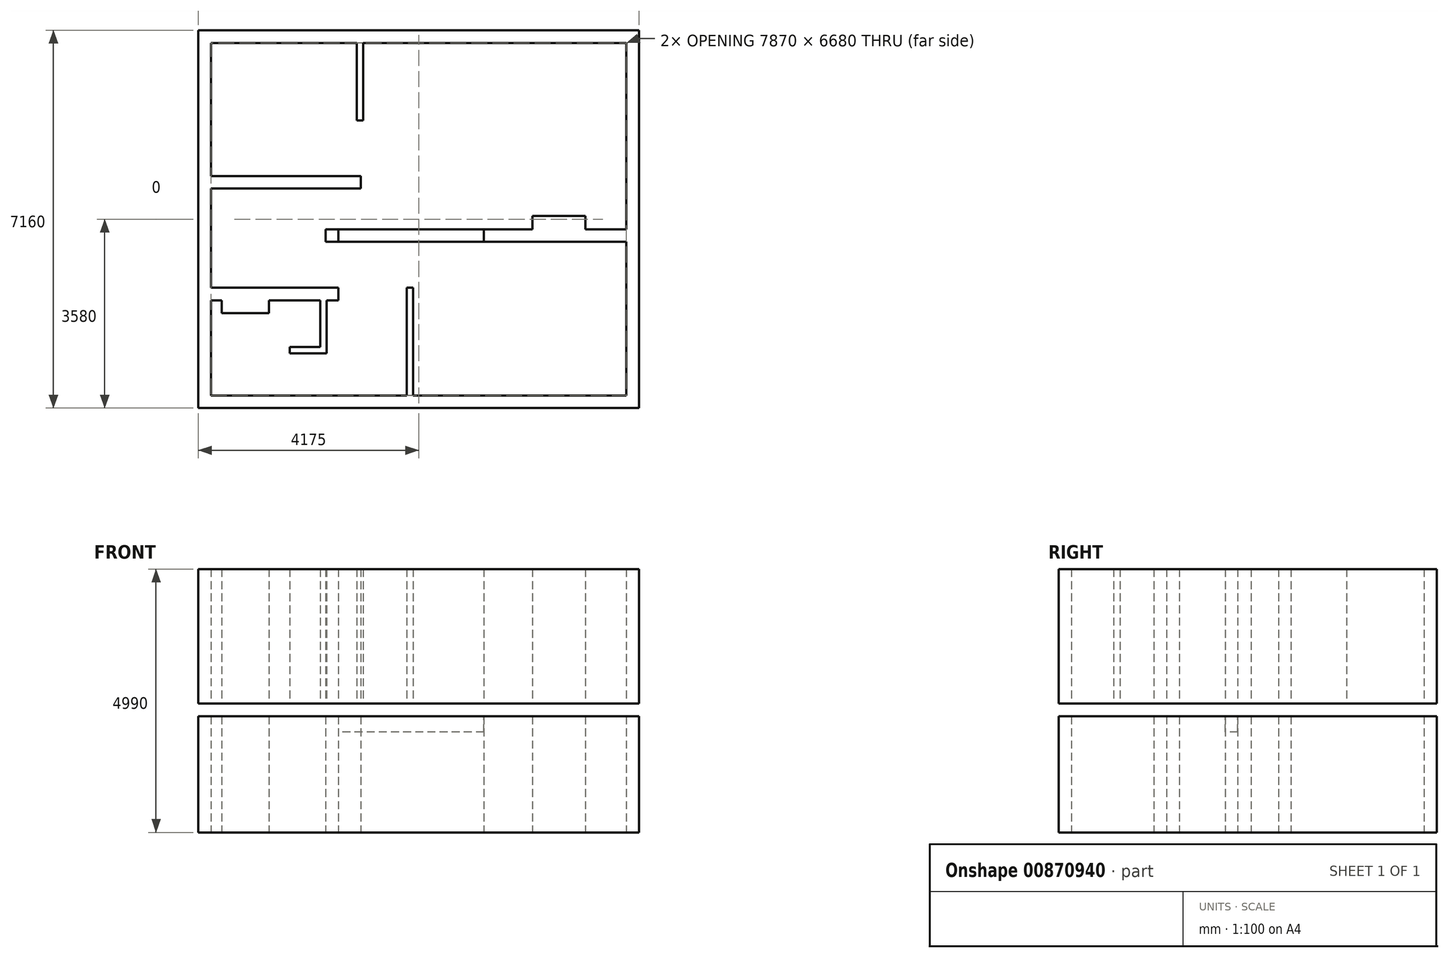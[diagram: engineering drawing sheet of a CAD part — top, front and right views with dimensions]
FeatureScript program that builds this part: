
annotation { "Feature Type Name" : "Feature", "Feature Type Description" : "" }
export const myFeature = defineFeature(function(context is Context, id is Id, definition is map)
    precondition{}
    {
        {
            var Q0;
            Q0=qCreatedBy(makeId("Top.planeOp"),FACE);
            var sketch = newSketch(context, id + "F0", { "sketchPlane" : qUnion([Q0])});
            skLineSegment(sketch, "E0.bottom", {"start": v(0, 0) * mm, "end": v(-8350, 0) * mm});
            skLineSegment(sketch, "E0.top", {"start": v(0, 7160) * mm, "end": v(-8350, 7160) * mm});
            skLineSegment(sketch, "E0.left", {"start": v(0, 0) * mm, "end": v(0, 7160) * mm});
            skLineSegment(sketch, "E0.right", {"start": v(-8350, 0) * mm, "end": v(-8350, 7160) * mm});
            skLineSegment(sketch, "E1.0", {"start": v(-240, 6920) * mm, "end": v(-8110, 6920) * mm});
            skLineSegment(sketch, "E1.1", {"start": v(-240, 240) * mm, "end": v(-240, 3150) * mm});
            skLineSegment(sketch, "E1.2", {"start": v(-240, 240) * mm, "end": v(-8110, 240) * mm});
            skLineSegment(sketch, "E1.3", {"start": v(-8110, 240) * mm, "end": v(-8110, 2040) * mm});
            skLineSegment(sketch, "E2", {"start": v(-8110, 2040) * mm, "end": v(-7910, 2040) * mm});
            skLineSegment(sketch, "E3", {"start": v(-7910, 2040) * mm, "end": v(-7910, 1800) * mm});
            skLineSegment(sketch, "E4", {"start": v(-7910, 1800) * mm, "end": v(-7010, 1800) * mm});
            skLineSegment(sketch, "E5", {"start": v(-7010, 1800) * mm, "end": v(-7010, 2040) * mm});
            skLineSegment(sketch, "E6", {"start": v(-7010, 2040) * mm, "end": v(-5700, 2040) * mm});
            skLineSegment(sketch, "E7", {"start": v(-5700, 2040) * mm, "end": v(-5700, 2280) * mm});
            skLineSegment(sketch, "E8", {"start": v(-5700, 2280) * mm, "end": v(-8110, 2280) * mm});
            skLineSegment(sketch, "E9.trimOffspring", {"start": v(-8110, 2280) * mm, "end": v(-8110, 4160) * mm});
            skLineSegment(sketch, "E10", {"start": v(-8110, 4160) * mm, "end": v(-5270, 4160) * mm});
            skLineSegment(sketch, "E11", {"start": v(-5270, 4160) * mm, "end": v(-5270, 4400) * mm});
            skLineSegment(sketch, "E12", {"start": v(-5270, 4400) * mm, "end": v(-8110, 4400) * mm});
            skLineSegment(sketch, "E13.trimOffspring", {"start": v(-8110, 4400) * mm, "end": v(-8110, 6920) * mm});
            skLineSegment(sketch, "E14", {"start": v(-240, 3150) * mm, "end": v(-2940, 3150) * mm});
            skLineSegment(sketch, "E15", {"start": v(-2940, 3150) * mm, "end": v(-2940, 3390) * mm});
            skLineSegment(sketch, "E16", {"start": v(-2940, 3390) * mm, "end": v(-2020, 3390) * mm});
            skLineSegment(sketch, "E17.trimOffspring", {"start": v(-240, 3390) * mm, "end": v(-240, 6920) * mm});
            skLineSegment(sketch, "E18", {"start": v(-2020, 3390) * mm, "end": v(-2020, 3640) * mm});
            skLineSegment(sketch, "E19", {"start": v(-2020, 3640) * mm, "end": v(-1020, 3640) * mm});
            skLineSegment(sketch, "E20", {"start": v(-1020, 3640) * mm, "end": v(-1020, 3390) * mm});
            skLineSegment(sketch, "E21.trimOffspring", {"start": v(-1020, 3390) * mm, "end": v(-240, 3390) * mm});
            skLineSegment(sketch, "E22.bottom", {"start": v(-5940, 3150) * mm, "end": v(-5700, 3150) * mm});
            skLineSegment(sketch, "E22.top", {"start": v(-5940, 3390) * mm, "end": v(-5700, 3390) * mm});
            skLineSegment(sketch, "E22.left", {"start": v(-5940, 3150) * mm, "end": v(-5940, 3390) * mm});
            skLineSegment(sketch, "E22.right", {"start": v(-5700, 3150) * mm, "end": v(-5700, 3390) * mm});
            skSolve(sketch);
        }
        {
            var Q0;
            Q0=makeQuery(id+"F0.imprint","IMPRINT",FACE,{"disambiguationData":[TD([[makeQuery(id+"F0.imprint","IMPRINT",EDGE,{"derivedFrom":sQuery(id+"F0.wireOp",EDGE,"E0.bottom")}),-1.0]])]});
            extrude(context, id + "F1", {"entities" : qUnion([Q0]), "depth" : 2200 * mm, "offsetDistance" : 25 * mm});
        }
        {
            var Q0;
            Q0=makeQuery(id+"F0.imprint","IMPRINT",FACE,{"disambiguationData":[TD([[makeQuery(id+"F0.imprint","IMPRINT",EDGE,{"derivedFrom":sQuery(id+"F0.wireOp",EDGE,"E22.bottom")}),1.0]])]});
            extrude(context, id + "F2", {"entities" : qUnion([Q0]), "depth" : 2200 * mm, "offsetDistance" : 25 * mm});
        }
        {
            var Q0;
            Q0=makeQuery(id+"F2.opExtrude","SWEPT_FACE",FACE,{"disambiguationData":[OSD([sQuery(id+"F0.wireOp",EDGE,"E22.right")])]});
            var sketch = newSketch(context, id + "F3", { "sketchPlane" : qUnion([Q0])});
            skLineSegment(sketch, "E23.0", {"start": v(3150, 2200) * mm, "end": v(3390, 2200) * mm});
            skLineSegment(sketch, "E24.0", {"start": v(3150, 2200) * mm, "end": v(3150, 0) * mm});
            skLineSegment(sketch, "E24.1", {"start": v(3390, 2200) * mm, "end": v(3390, 0) * mm});
            skLineSegment(sketch, "E25", {"start": v(3150, 1900) * mm, "end": v(3390, 1900) * mm});
            skSolve(sketch);
        }
        {
            var Q0;
            {var subQ0=sQuery(id+"F3.wireOp",EDGE,"E23.0");Q0=makeQuery(id+"F3.imprint","IMPRINT",FACE,{"disambiguationData":[TD([[makeQuery(id+"F3.imprint","IMPRINT",EDGE,{"derivedFrom":subQ0}),-1.0]])]});}
            extrude(context, id + "F4", {"entities" : qUnion([Q0]), "endBound" : BoundingType.UP_TO_NEXT, "depth" : 25 * mm, "offsetDistance" : 25 * mm});
        }
        {
            var Q0;
            Q0=makeQuery(id+"F1.opExtrude","CAP_FACE",FACE,{"disambiguationData":[OSD([sQuery(id+"F0.wireOp",EDGE,"E0.bottom"),sQuery(id+"F0.wireOp",EDGE,"E0.top"),sQuery(id+"F0.wireOp",EDGE,"E0.left"),sQuery(id+"F0.wireOp",EDGE,"E0.right"),sQuery(id+"F0.wireOp",EDGE,"E1.0"),sQuery(id+"F0.wireOp",EDGE,"E1.1"),sQuery(id+"F0.wireOp",EDGE,"E1.2"),sQuery(id+"F0.wireOp",EDGE,"E1.3"),sQuery(id+"F0.wireOp",EDGE,"E2"),sQuery(id+"F0.wireOp",EDGE,"E3"),sQuery(id+"F0.wireOp",EDGE,"E4"),sQuery(id+"F0.wireOp",EDGE,"E5"),sQuery(id+"F0.wireOp",EDGE,"E6"),sQuery(id+"F0.wireOp",EDGE,"E7"),sQuery(id+"F0.wireOp",EDGE,"E8"),sQuery(id+"F0.wireOp",EDGE,"E9.trimOffspring"),sQuery(id+"F0.wireOp",EDGE,"E10"),sQuery(id+"F0.wireOp",EDGE,"E11"),sQuery(id+"F0.wireOp",EDGE,"E12"),sQuery(id+"F0.wireOp",EDGE,"E13.trimOffspring"),sQuery(id+"F0.wireOp",EDGE,"E14"),sQuery(id+"F0.wireOp",EDGE,"E15"),sQuery(id+"F0.wireOp",EDGE,"E16"),sQuery(id+"F0.wireOp",EDGE,"E17.trimOffspring"),sQuery(id+"F0.wireOp",EDGE,"E18"),sQuery(id+"F0.wireOp",EDGE,"E19"),sQuery(id+"F0.wireOp",EDGE,"E20"),sQuery(id+"F0.wireOp",EDGE,"E21.trimOffspring")])],"isStart":false});
            cPlane(context, id + "F5", {"entities" : qUnion([Q0]), "cplaneType" : CPlaneType.OFFSET, "offset" : 240 * mm, "width" : 150 * mm, "height" : 150 * mm});
        }
        {
            var Q0;
            Q0=qCreatedBy(id+"F5.planeOp",FACE);
            var sketch = newSketch(context, id + "F6", { "sketchPlane" : qUnion([Q0])});
            skLineSegment(sketch, "E26.0", {"start": v(0, 7160) * mm, "end": v(-8350, 7160) * mm});
            skLineSegment(sketch, "E26.1", {"start": v(-8350, 0) * mm, "end": v(-8350, 7160) * mm});
            skLineSegment(sketch, "E26.2", {"start": v(0, 0) * mm, "end": v(-8350, 0) * mm});
            skLineSegment(sketch, "E26.3", {"start": v(0, 0) * mm, "end": v(0, 7160) * mm});
            skLineSegment(sketch, "E27.0", {"start": v(-8110, 240) * mm, "end": v(-8110, 2040) * mm});
            skLineSegment(sketch, "E27.1", {"start": v(-240, 240) * mm, "end": v(-4280, 240) * mm});
            skLineSegment(sketch, "E27.2", {"start": v(-8110, 2040) * mm, "end": v(-7910, 2040) * mm});
            skLineSegment(sketch, "E27.3", {"start": v(-7910, 2040) * mm, "end": v(-7910, 1800) * mm});
            skLineSegment(sketch, "E27.4", {"start": v(-7910, 1800) * mm, "end": v(-7010, 1800) * mm});
            skLineSegment(sketch, "E27.5", {"start": v(-7010, 1800) * mm, "end": v(-7010, 2040) * mm});
            skLineSegment(sketch, "E27.6", {"start": v(-7010, 2040) * mm, "end": v(-6040, 2040) * mm});
            skLineSegment(sketch, "E27.7", {"start": v(-5700, 2280) * mm, "end": v(-8110, 2280) * mm});
            skLineSegment(sketch, "E27.8", {"start": v(-8110, 2280) * mm, "end": v(-8110, 4160) * mm});
            skLineSegment(sketch, "E27.9", {"start": v(-8110, 4160) * mm, "end": v(-5270, 4160) * mm});
            skLineSegment(sketch, "E27.10", {"start": v(-5270, 4400) * mm, "end": v(-8110, 4400) * mm});
            skLineSegment(sketch, "E27.11", {"start": v(-8110, 4400) * mm, "end": v(-8110, 6920) * mm});
            skLineSegment(sketch, "E27.12", {"start": v(-240, 6920) * mm, "end": v(-5230, 6920) * mm});
            skLineSegment(sketch, "E27.13", {"start": v(-5940, 3150) * mm, "end": v(-5940, 3390) * mm});
            skLineSegment(sketch, "E27.14", {"start": v(-5940, 3150) * mm, "end": v(-5700, 3150) * mm});
            skLineSegment(sketch, "E27.15", {"start": v(-5940, 3390) * mm, "end": v(-5700, 3390) * mm});
            skLineSegment(sketch, "E27.16", {"start": v(-5700, 3150) * mm, "end": v(-5700, 3390) * mm});
            skLineSegment(sketch, "E27.17", {"start": v(-240, 3150) * mm, "end": v(-2940, 3150) * mm});
            skLineSegment(sketch, "E27.18", {"start": v(-2940, 3390) * mm, "end": v(-2020, 3390) * mm});
            skLineSegment(sketch, "E27.19", {"start": v(-2940, 3150) * mm, "end": v(-2940, 3390) * mm});
            skLineSegment(sketch, "E27.20", {"start": v(-2020, 3390) * mm, "end": v(-2020, 3640) * mm});
            skLineSegment(sketch, "E27.21", {"start": v(-2020, 3640) * mm, "end": v(-1020, 3640) * mm});
            skLineSegment(sketch, "E27.22", {"start": v(-1020, 3640) * mm, "end": v(-1020, 3390) * mm});
            skLineSegment(sketch, "E27.23", {"start": v(-1020, 3390) * mm, "end": v(-240, 3390) * mm});
            skLineSegment(sketch, "E27.24", {"start": v(-240, 3390) * mm, "end": v(-240, 6920) * mm});
            skLineSegment(sketch, "E27.25", {"start": v(-240, 240) * mm, "end": v(-240, 3150) * mm});
            skLineSegment(sketch, "E28", {"start": v(-6040, 2040) * mm, "end": v(-6040, 1160) * mm});
            skLineSegment(sketch, "E29", {"start": v(-6040, 1160) * mm, "end": v(-6620, 1160) * mm});
            skLineSegment(sketch, "E30", {"start": v(-6620, 1160) * mm, "end": v(-6620, 1040) * mm});
            skLineSegment(sketch, "E31", {"start": v(-6620, 1040) * mm, "end": v(-5920, 1040) * mm});
            skLineSegment(sketch, "E32", {"start": v(-5920, 1040) * mm, "end": v(-5920, 2040) * mm});
            skLineSegment(sketch, "E33", {"start": v(-5350, 6920) * mm, "end": v(-5350, 5450) * mm});
            skLineSegment(sketch, "E34", {"start": v(-5350, 5450) * mm, "end": v(-5230, 5450) * mm});
            skLineSegment(sketch, "E35", {"start": v(-5230, 5450) * mm, "end": v(-5230, 6920) * mm});
            skLineSegment(sketch, "E36", {"start": v(-4400, 240) * mm, "end": v(-4400, 2280) * mm});
            skLineSegment(sketch, "E37", {"start": v(-4400, 2280) * mm, "end": v(-4280, 2280) * mm});
            skLineSegment(sketch, "E38", {"start": v(-4280, 2280) * mm, "end": v(-4280, 1800) * mm});
            skLineSegment(sketch, "E39", {"start": v(-4280, 1680) * mm, "end": v(-4280, 240) * mm});
            skLineSegment(sketch, "E40.trimOffspring", {"start": v(-4400, 240) * mm, "end": v(-8110, 240) * mm});
            skLineSegment(sketch, "E41.trimOffspring", {"start": v(-5350, 6920) * mm, "end": v(-8110, 6920) * mm});
            skLineSegment(sketch, "E42.trimOffspring", {"start": v(-5920, 2040) * mm, "end": v(-5700, 2040) * mm});
            skLineSegment(sketch, "E43", {"start": v(-5700, 2040) * mm, "end": v(-5700, 2280) * mm});
            skLineSegment(sketch, "E44", {"start": v(-5270, 4160) * mm, "end": v(-5270, 4400) * mm});
            skLineSegment(sketch, "E45", {"start": v(-4280, 1680) * mm, "end": v(-4280, 1800) * mm});
            skSolve(sketch);
        }
        {
            var Q0;
            Q0=makeQuery(id+"F6.imprint","IMPRINT",FACE,{"disambiguationData":[TD([[makeQuery(id+"F6.imprint","IMPRINT",EDGE,{"derivedFrom":sQuery(id+"F6.wireOp",EDGE,"E26.0")}),1.0]])]});
            var Q1;
            Q1=makeQuery(id+"F6.imprint","IMPRINT",FACE,{"disambiguationData":[TD([[makeQuery(id+"F6.imprint","IMPRINT",EDGE,{"derivedFrom":sQuery(id+"F6.wireOp",EDGE,"E27.13")}),-1.0]])]});
            extrude(context, id + "F7", {"entities" : qUnion([Q0, Q1]), "depth" : 2550 * mm, "offsetDistance" : 25 * mm});
        }
    });
